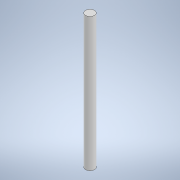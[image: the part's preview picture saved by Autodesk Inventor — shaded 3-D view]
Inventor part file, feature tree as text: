
AUTODESK INVENTOR PART (.ipt)
format: ipt  version: 2022 (Build 260153000, 153)  size: 93,184 bytes
history: native  units: in
note: dims shown in document units (in); Inventor stores cm internally (conversion verified against a paired STEP export)
features: extrude x1, sketch x1
ambient origin geometry x8: Origin, YZ Plane, XZ Plane, XY Plane, X Axis, Y Axis, Z Axis, Center Point
bodies: Solid1 (feature_tree)
feature tree (2):
  extrude  "Extrusion1"  Depth=1.5in TaperAngle=0.0deg
  sketch  "Sketch1"  dims[d0=0.1in d1=1.5in d2=0.0in]
